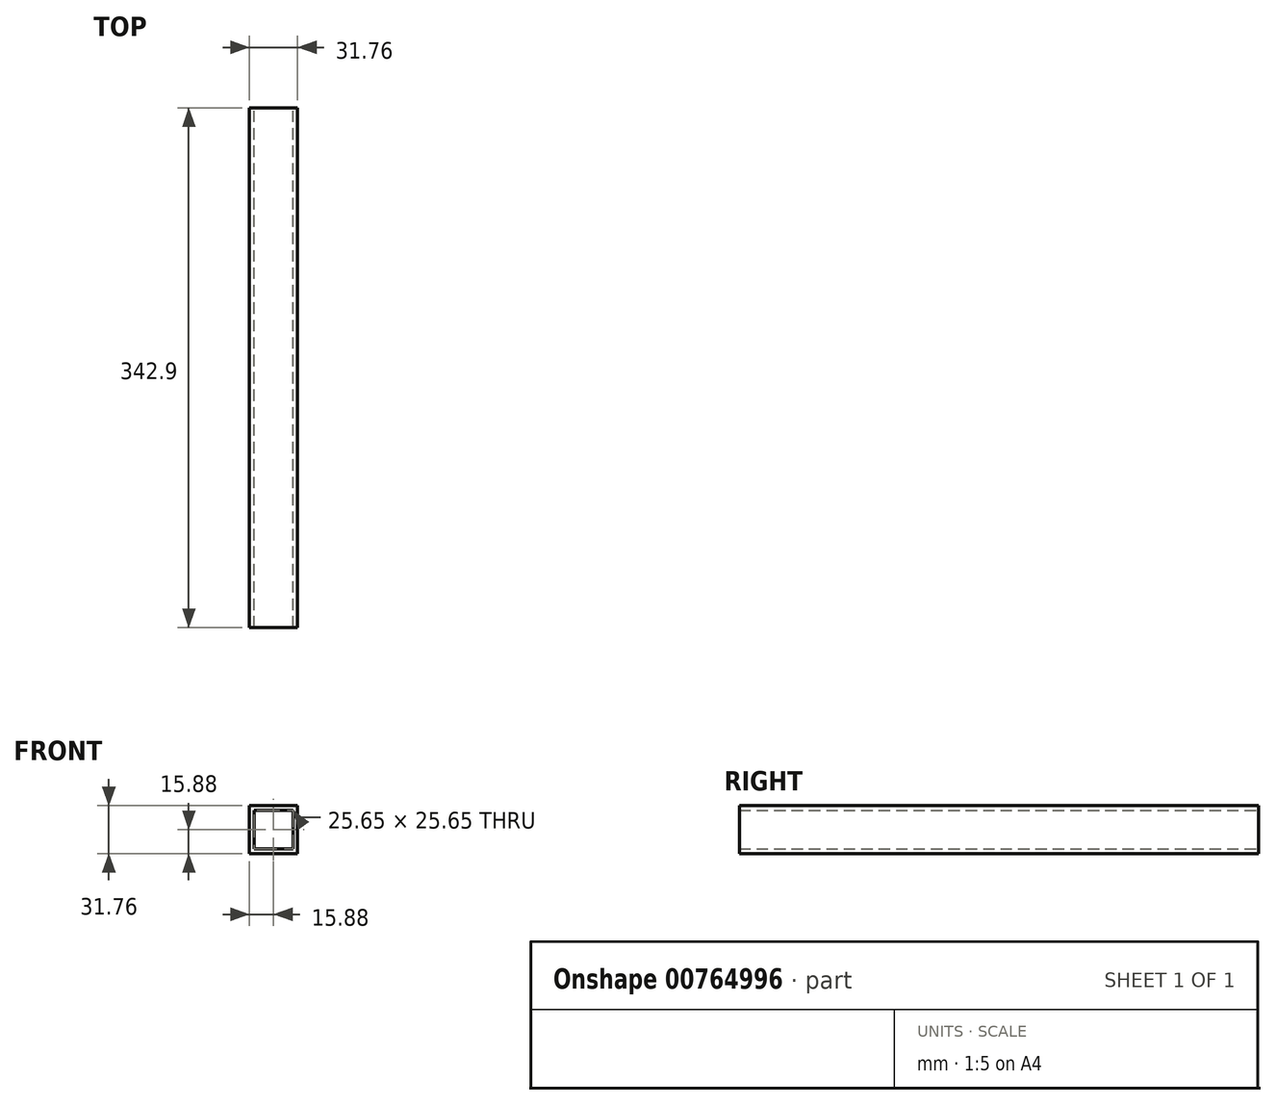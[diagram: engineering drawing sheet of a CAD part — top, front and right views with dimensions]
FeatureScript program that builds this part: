
annotation { "Feature Type Name" : "Feature", "Feature Type Description" : "" }
export const myFeature = defineFeature(function(context is Context, id is Id, definition is map)
    precondition{}
    {
        {
            var Q0;
            Q0=qCreatedBy(makeId("Front.planeOp"),FACE);
            var sketch = newSketch(context, id + "F0", { "sketchPlane" : qUnion([Q0])});
            skLineSegment(sketch, "E0.bottom", {"start": v(15.88, 15.88) * mm, "end": v(-15.88, 15.88) * mm});
            skLineSegment(sketch, "E0.top", {"start": v(15.88, -15.88) * mm, "end": v(-15.88, -15.88) * mm});
            skLineSegment(sketch, "E0.left", {"start": v(15.88, 15.88) * mm, "end": v(15.88, -15.88) * mm});
            skLineSegment(sketch, "E0.right", {"start": v(-15.88, 15.87) * mm, "end": v(-15.88, -15.88) * mm});
            skPoint(sketch, "E0.middle", {"position": v(0, 0) * mm});
            skLineSegment(sketch, "E1.0", {"start": v(12.83, -12.83) * mm, "end": v(-12.83, -12.83) * mm});
            skLineSegment(sketch, "E1.1", {"start": v(12.83, 12.83) * mm, "end": v(12.83, -12.83) * mm});
            skLineSegment(sketch, "E1.2", {"start": v(12.83, 12.83) * mm, "end": v(-12.83, 12.83) * mm});
            skLineSegment(sketch, "E1.3", {"start": v(-12.83, 12.83) * mm, "end": v(-12.83, -12.83) * mm});
            skSolve(sketch);
        }
        {
            var Q0;
            Q0 = qSketchRegion(id + "F0", true);
            extrude(context, id + "F1", {"entities" : qUnion([Q0]), "depth" : 342.9 * mm, "offsetDistance" : 25.4 * mm});
        }
    });
